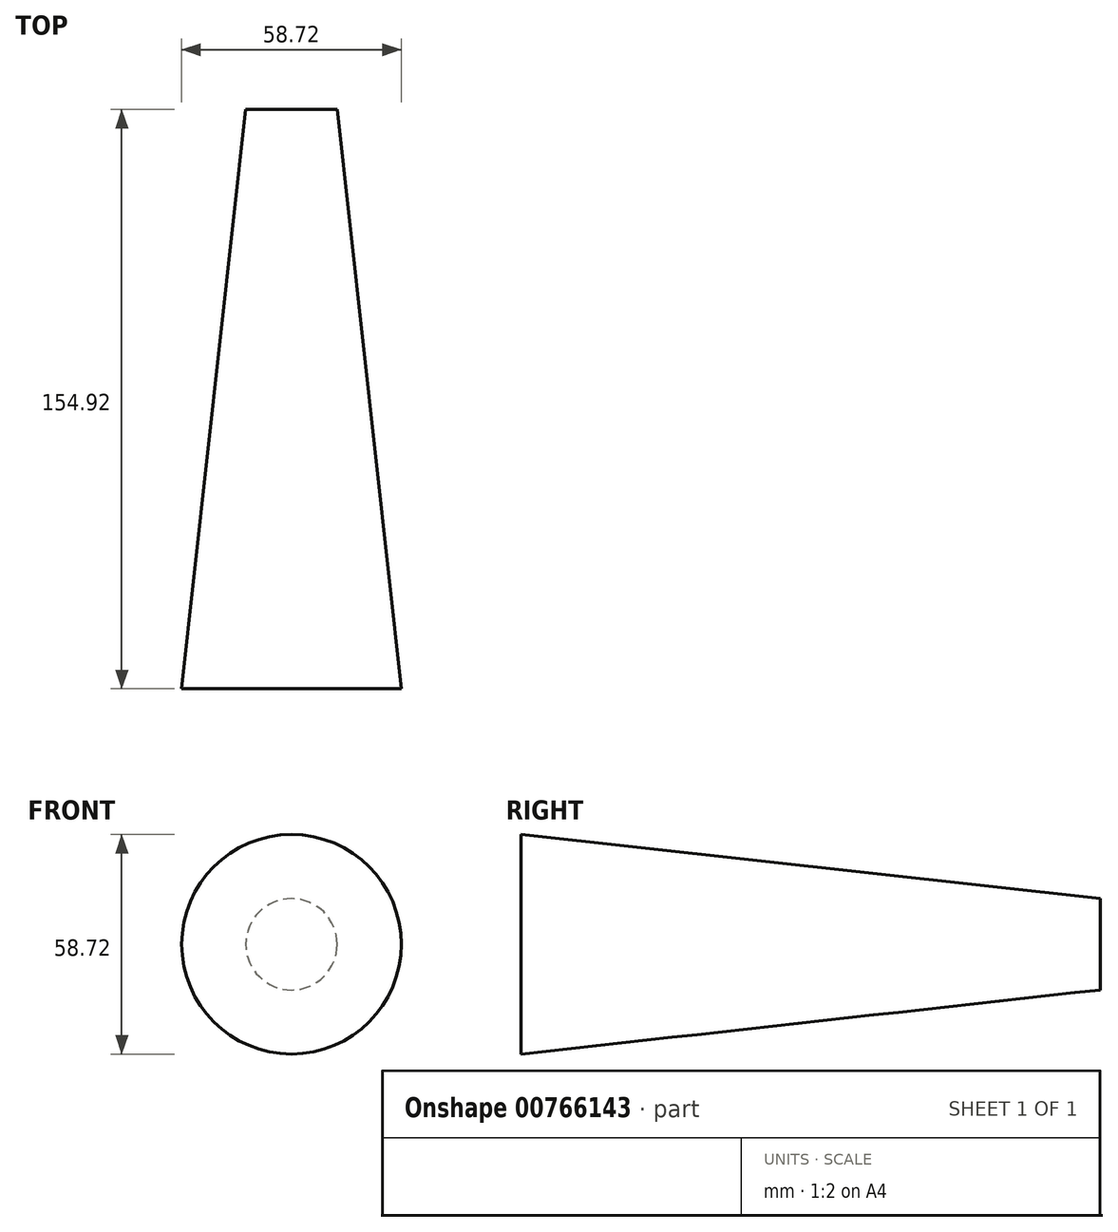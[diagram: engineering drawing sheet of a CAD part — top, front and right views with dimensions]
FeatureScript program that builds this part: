
annotation { "Feature Type Name" : "Feature", "Feature Type Description" : "" }
export const myFeature = defineFeature(function(context is Context, id is Id, definition is map)
    precondition{}
    {
        {
            var Q0;
            Q0=qCreatedBy(makeId("Front.planeOp"),FACE);
            var sketch = newSketch(context, id + "F0", { "sketchPlane" : qUnion([Q0])});
            skCircle(sketch, "E0", {"center": v(0, 0) * mm, "radius": 12.21 * mm});
            skSolve(sketch);
        }
        {
            var Q0;
            Q0=qCreatedBy(makeId("Front.planeOp"),FACE);
            cPlane(context, id + "F1", {"entities" : qUnion([Q0]), "cplaneType" : CPlaneType.OFFSET, "offset" : 154.92 * mm, "width" : 152.4 * mm, "height" : 152.4 * mm});
        }
        {
            var Q0;
            Q0=qCreatedBy(id+"F1.planeOp",FACE);
            var sketch = newSketch(context, id + "F2", { "sketchPlane" : qUnion([Q0])});
            skCircle(sketch, "E1", {"center": v(0, 0) * mm, "radius": 29.36 * mm});
            skSolve(sketch);
        }
        {
            var Q0;
            Q0 = qSketchRegion(id + "F2", true);
            var Q1;
            Q1 = qSketchRegion(id + "F0", true);
            loft(context, id + "F3", {"sheetProfilesArray" : [{ "sheetProfileEntities" : qUnion([Q0]) }, { "sheetProfileEntities" : qUnion([Q1]) }]});
        }
    });
